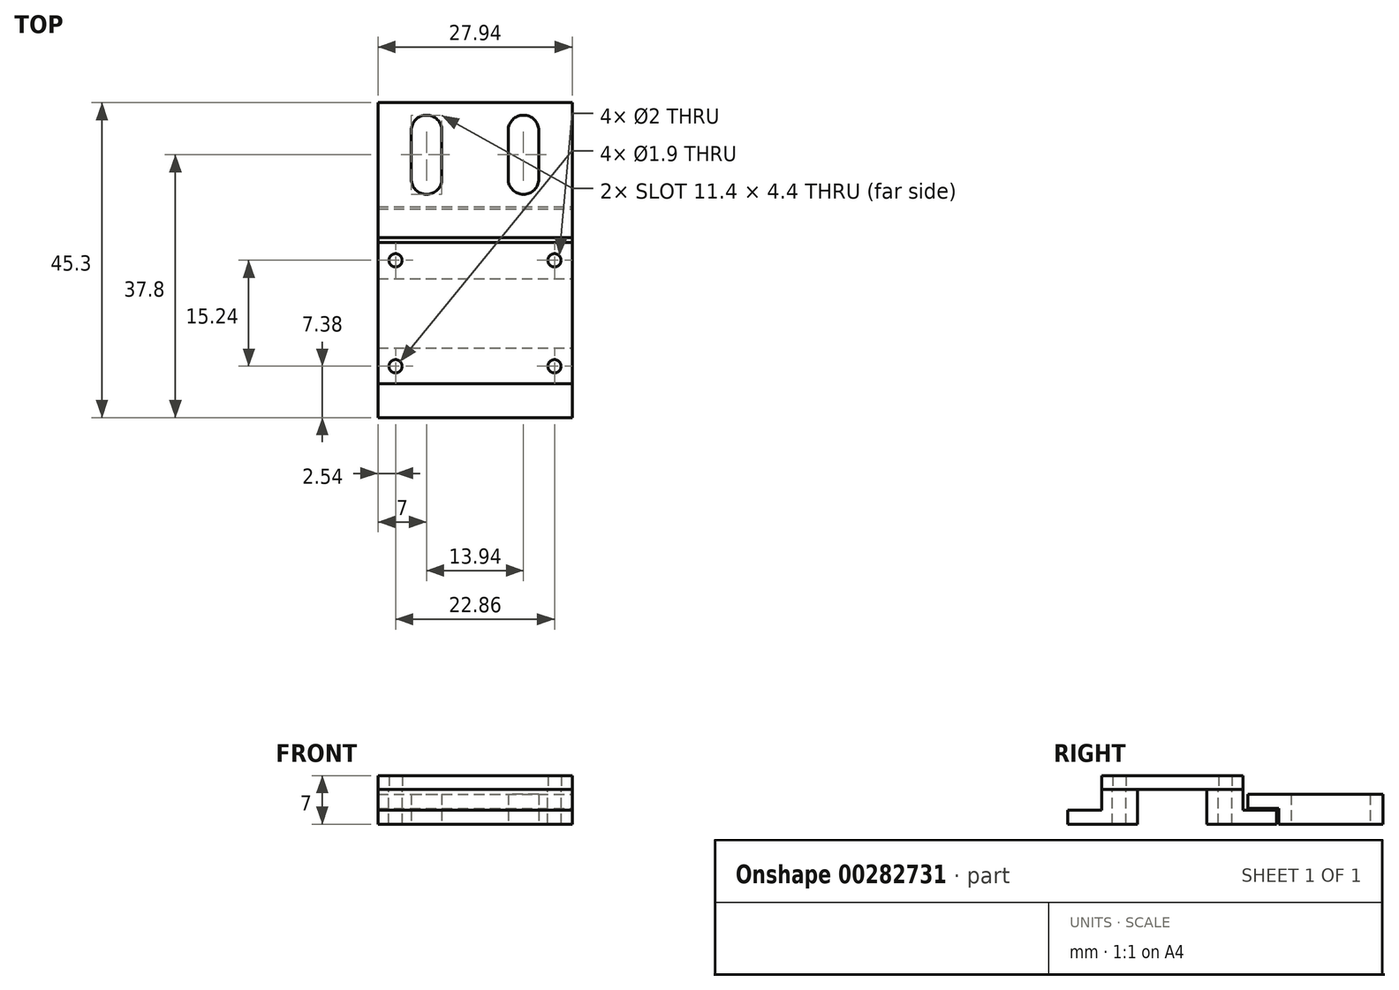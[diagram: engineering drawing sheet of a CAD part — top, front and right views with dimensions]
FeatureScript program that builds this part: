
annotation { "Feature Type Name" : "Feature", "Feature Type Description" : "" }
export const myFeature = defineFeature(function(context is Context, id is Id, definition is map)
    precondition{}
    {
        {
            var Q0;
            Q0=qCreatedBy(makeId("Top.planeOp"),FACE);
            var sketch = newSketch(context, id + "F0", { "sketchPlane" : qUnion([Q0])});
            skLineSegment(sketch, "E0.bottom", {"start": v(13.97, -10.16) * mm, "end": v(-13.97, -10.16) * mm});
            skLineSegment(sketch, "E0.top", {"start": v(13.97, 10.16) * mm, "end": v(-13.97, 10.16) * mm});
            skLineSegment(sketch, "E0.left", {"start": v(13.97, -10.16) * mm, "end": v(13.97, 10.16) * mm});
            skLineSegment(sketch, "E0.right", {"start": v(-13.97, -10.16) * mm, "end": v(-13.97, 10.16) * mm});
            skPoint(sketch, "E0.middle", {"position": v(0, 0) * mm});
            skLineSegment(sketch, "E1.bottom", {"start": v(11.43, -7.62) * mm, "end": v(-11.43, -7.62) * mm, "construction": true});
            skLineSegment(sketch, "E1.top", {"start": v(11.43, 7.62) * mm, "end": v(-11.43, 7.62) * mm, "construction": true});
            skLineSegment(sketch, "E1.left", {"start": v(11.43, -7.62) * mm, "end": v(11.43, 7.62) * mm, "construction": true});
            skLineSegment(sketch, "E1.right", {"start": v(-11.43, -7.62) * mm, "end": v(-11.43, 7.62) * mm, "construction": true});
            skCircle(sketch, "E2", {"center": v(-11.43, 7.62) * mm, "radius": 0.95 * mm});
            skCircle(sketch, "E3", {"center": v(-11.43, -7.62) * mm, "radius": 0.95 * mm});
            skCircle(sketch, "E4", {"center": v(11.43, 7.62) * mm, "radius": 0.95 * mm});
            skCircle(sketch, "E5", {"center": v(11.43, -7.62) * mm, "radius": 0.95 * mm});
            skSolve(sketch);
        }
        {
            var Q0;
            Q0 = qSketchRegion(id + "F0", true);
            extrude(context, id + "F1", {"entities" : qUnion([Q0]), "depth" : 2 * mm});
        }
        {
            var Q0;
            Q0=makeQuery(id+"F0.imprint","IMPRINT",FACE,{"disambiguationData":[TD([[makeQuery(id+"F0.imprint","IMPRINT",EDGE,{"derivedFrom":sQuery(id+"F0.wireOp",EDGE,"E0.bottom")}),-1.0]])]});
            var sketch = newSketch(context, id + "F2", { "sketchPlane" : qUnion([Q0])});
            skLineSegment(sketch, "E6.top", {"start": v(-13.97, -10.16) * mm, "end": v(13.97, -10.16) * mm});
            skLineSegment(sketch, "E6.left", {"start": v(-13.97, -5) * mm, "end": v(-13.97, -10.16) * mm});
            skLineSegment(sketch, "E6.right", {"start": v(13.97, -5) * mm, "end": v(13.97, -10.16) * mm});
            skLineSegment(sketch, "E7", {"start": v(-13.97, -5) * mm, "end": v(13.97, -5) * mm});
            skLineSegment(sketch, "E8.MirrorCS", {"start": v(-13.97, 10.16) * mm, "end": v(13.97, 10.16) * mm});
            skLineSegment(sketch, "E9.MirrorCS", {"start": v(-13.97, 5) * mm, "end": v(-13.97, 10.16) * mm});
            skLineSegment(sketch, "E10.MirrorCS", {"start": v(-13.97, 5) * mm, "end": v(13.97, 5) * mm});
            skLineSegment(sketch, "E11.MirrorCS", {"start": v(13.97, 5) * mm, "end": v(13.97, 10.16) * mm});
            skSolve(sketch);
        }
        {
            var Q0;
            Q0 = qSketchRegion(id + "F2", true);
            extrude(context, id + "F3", {"entities" : qUnion([Q0]), "oppositeDirection" : true, "depth" : 3 * mm});
        }
        {
            var Q0;
            Q0=makeQuery(id+"F3.opExtrude","CAP_FACE",FACE,{"disambiguationData":[OSD([sQuery(id+"F2.wireOp",EDGE,"E6.top"),sQuery(id+"F2.wireOp",EDGE,"E6.left"),sQuery(id+"F2.wireOp",EDGE,"E6.right"),sQuery(id+"F2.wireOp",EDGE,"E7")])],"isStart":false});
            var sketch = newSketch(context, id + "F4", { "sketchPlane" : qUnion([Q0])});
            skLineSegment(sketch, "E12.bottom", {"start": v(-13.97, 5) * mm, "end": v(13.97, 5) * mm});
            skLineSegment(sketch, "E12.top", {"start": v(-13.97, 15) * mm, "end": v(13.97, 15) * mm});
            skLineSegment(sketch, "E12.left", {"start": v(-13.97, 5) * mm, "end": v(-13.97, 15) * mm});
            skLineSegment(sketch, "E12.right", {"start": v(13.97, 5) * mm, "end": v(13.97, 15) * mm});
            skSolve(sketch);
        }
        {
            var Q0;
            Q0 = qSketchRegion(id + "F4", true);
            extrude(context, id + "F5", {"entities" : qUnion([Q0]), "operationType" : NewBodyOperationType.ADD, "depth" : 2 * mm});
        }
        {
            var Q0;
            Q0=makeQuery(id+"F3.opExtrude","CAP_FACE",FACE,{"disambiguationData":[OSD([sQuery(id+"F2.wireOp",EDGE,"E8.MirrorCS"),sQuery(id+"F2.wireOp",EDGE,"E9.MirrorCS"),sQuery(id+"F2.wireOp",EDGE,"E10.MirrorCS"),sQuery(id+"F2.wireOp",EDGE,"E11.MirrorCS")])],"isStart":false});
            var sketch = newSketch(context, id + "F6", { "sketchPlane" : qUnion([Q0])});
            skLineSegment(sketch, "E13.bottom", {"start": v(-13.97, -5) * mm, "end": v(13.97, -5) * mm});
            skLineSegment(sketch, "E13.top", {"start": v(-13.97, -15) * mm, "end": v(13.97, -15) * mm});
            skLineSegment(sketch, "E13.left", {"start": v(-13.97, -5) * mm, "end": v(-13.97, -15) * mm});
            skLineSegment(sketch, "E13.right", {"start": v(13.97, -5) * mm, "end": v(13.97, -15) * mm});
            skSolve(sketch);
        }
        {
            var Q0;
            Q0 = qSketchRegion(id + "F6", true);
            extrude(context, id + "F7", {"entities" : qUnion([Q0]), "operationType" : NewBodyOperationType.ADD, "depth" : 2 * mm});
        }
        {
            var Q0;
            Q0=makeQuery(id+"F7.opExtrude","CAP_FACE",FACE,{"disambiguationData":[OSD([sQuery(id+"F6.wireOp",EDGE,"E13.bottom"),sQuery(id+"F6.wireOp",EDGE,"E13.top"),sQuery(id+"F6.wireOp",EDGE,"E13.left"),sQuery(id+"F6.wireOp",EDGE,"E13.right")])],"isStart":false});
            var sketch = newSketch(context, id + "F8", { "sketchPlane" : qUnion([Q0])});
            skLineSegment(sketch, "E14.bottom", {"start": v(-13.97, -15.3) * mm, "end": v(13.97, -15.3) * mm});
            skLineSegment(sketch, "E14.top", {"start": v(-13.97, -30.3) * mm, "end": v(13.97, -30.3) * mm});
            skLineSegment(sketch, "E14.left", {"start": v(-13.97, -15.3) * mm, "end": v(-13.97, -30.3) * mm});
            skLineSegment(sketch, "E14.right", {"start": v(13.97, -15.3) * mm, "end": v(13.97, -30.3) * mm});
            skLineSegment(sketch, "E15", {"start": v(-13.97, -22.8) * mm, "end": v(13.97, -22.8) * mm, "construction": true});
            skLineSegment(sketch, "E16", {"start": v(-6.97, -15.3) * mm, "end": v(-6.97, -30.3) * mm, "construction": true});
            skLineSegment(sketch, "E17", {"start": v(6.97, -15.3) * mm, "end": v(6.97, -30.3) * mm, "construction": true});
            skPoint(sketch, "E18", {"position": v(-6.97, -22.8) * mm});
            skPoint(sketch, "E19", {"position": v(6.97, -22.8) * mm});
            skPoint(sketch, "E20", {"position": v(-6.97, -19.3) * mm});
            skPoint(sketch, "E21", {"position": v(-6.97, -26.3) * mm});
            skArc(sketch, "E22", {"start": v(-4.77, -19.3) * mm, "mid": v(-6.97, -17.1) * mm, "end": v(-9.17, -19.3) * mm});
            skArc(sketch, "E23", {"start": v(-9.17, -26.3) * mm, "mid": v(-6.97, -28.5) * mm, "end": v(-4.77, -26.3) * mm});
            skLineSegment(sketch, "E24", {"start": v(-9.17, -19.3) * mm, "end": v(-9.17, -26.3) * mm});
            skLineSegment(sketch, "E25", {"start": v(-4.77, -19.3) * mm, "end": v(-4.77, -26.3) * mm});
            skLineSegment(sketch, "E26.MirrorCS", {"start": v(9.17, -19.3) * mm, "end": v(9.17, -26.3) * mm});
            skLineSegment(sketch, "E27.MirrorCS", {"start": v(4.77, -19.3) * mm, "end": v(4.77, -26.3) * mm});
            skArc(sketch, "E28.MirrorCS", {"start": v(4.77, -19.3) * mm, "mid": v(6.97, -17.1) * mm, "end": v(9.17, -19.3) * mm});
            skArc(sketch, "E29.MirrorCS", {"start": v(9.17, -26.3) * mm, "mid": v(6.97, -28.5) * mm, "end": v(4.77, -26.3) * mm});
            skSolve(sketch);
        }
        {
            var Q0;
            Q0 = qSketchRegion(id + "F8", true);
            extrude(context, id + "F9", {"entities" : qUnion([Q0]), "oppositeDirection" : true, "depth" : 2.3 * mm});
        }
        {
            var Q0;
            Q0=makeQuery(id+"F9.opExtrude","CAP_FACE",FACE,{"disambiguationData":[OSD([sQuery(id+"F8.wireOp",EDGE,"E14.bottom"),sQuery(id+"F8.wireOp",EDGE,"E14.top"),sQuery(id+"F8.wireOp",EDGE,"E14.left"),sQuery(id+"F8.wireOp",EDGE,"E14.right")])],"isStart":false});
            var sketch = newSketch(context, id + "F10", { "sketchPlane" : qUnion([Q0])});
            skLineSegment(sketch, "E30.bottom", {"start": v(13.97, 30.3) * mm, "end": v(-13.97, 30.3) * mm});
            skLineSegment(sketch, "E30.top", {"start": v(13.97, 10.9) * mm, "end": v(-13.97, 10.9) * mm});
            skLineSegment(sketch, "E30.left", {"start": v(13.97, 30.3) * mm, "end": v(13.97, 10.9) * mm});
            skLineSegment(sketch, "E30.right", {"start": v(-13.97, 30.3) * mm, "end": v(-13.97, 10.9) * mm});
            skSolve(sketch);
        }
        {
            var Q0;
            Q0 = qSketchRegion(id + "F10", true);
            extrude(context, id + "F11", {"entities" : qUnion([Q0]), "operationType" : NewBodyOperationType.ADD, "depth" : 2 * mm});
        }
        {
            var Q0;
            Q0=sQuery(id+"F0.wireOp",VERTEX,"E2.center");
            var Q1;
            Q1=sQuery(id+"F0.wireOp",VERTEX,"E1.top.start");
            var Q2;
            Q2=sQuery(id+"F0.wireOp",VERTEX,"E5.center");
            var Q3;
            Q3=sQuery(id+"F0.wireOp",VERTEX,"E1.bottom.end");
            var Q4;
            Q4=makeQuery(id+"F3.opExtrude","SWEPT_BODY",BODY,{"disambiguationData":[OSD([sQuery(id+"F2.wireOp",EDGE,"E6.top"),sQuery(id+"F2.wireOp",EDGE,"E6.left"),sQuery(id+"F2.wireOp",EDGE,"E6.right"),sQuery(id+"F2.wireOp",EDGE,"E7")])]});
            var Q5;
            Q5=makeQuery(id+"F3.opExtrude","SWEPT_BODY",BODY,{"disambiguationData":[OSD([sQuery(id+"F2.wireOp",EDGE,"E8.MirrorCS"),sQuery(id+"F2.wireOp",EDGE,"E9.MirrorCS"),sQuery(id+"F2.wireOp",EDGE,"E10.MirrorCS"),sQuery(id+"F2.wireOp",EDGE,"E11.MirrorCS")])]});
            hole(context, id + "F12", {"style" : HoleStyle.SIMPLE, "endStyle" : HoleEndStyle.BLIND, "holeDiameter" : 2 * mm, "holeDepth" : 20 * mm, "tappedDepth" : 12 * mm, "tapClearance" : 3, "startFromSketch" : true, "locations" : qUnion([Q0, Q1, Q2, Q3]), "scope" : qUnion([Q4, Q5])});
        }
        {
            var Q0;
            Q0=sQuery(id+"F8.wireOp",VERTEX,"E18");
            var Q1;
            Q1=sQuery(id+"F8.wireOp",VERTEX,"E19");
            var Q2;
            Q2=makeQuery(id+"F9.opExtrude","SWEPT_BODY",BODY,{"disambiguationData":[OSD([sQuery(id+"F8.wireOp",EDGE,"E14.bottom"),sQuery(id+"F8.wireOp",EDGE,"E14.top"),sQuery(id+"F8.wireOp",EDGE,"E14.left"),sQuery(id+"F8.wireOp",EDGE,"E14.right")])]});
            hole(context, id + "F13", {"style" : HoleStyle.SIMPLE, "endStyle" : HoleEndStyle.BLIND, "standardTappedOrClearance" : lookupTablePath({ "standard" : "ISO", "fit" : "Normal", "size" : "M4", "type" : "Clearance" }), "standardBlindInLast" : lookupTablePath({ "fit" : "Standard", "standard" : "ISO", "size" : "M4", "type" : "Clearance" }), "holeDiameter" : 4.4 * mm, "holeDepth" : 20 * mm, "tappedDepth" : 12 * mm, "tapClearance" : 3, "locations" : qUnion([Q0, Q1]), "scope" : qUnion([Q2])});
        }
        {
            var Q0;
            Q0=makeQuery(id+"F8.imprint","IMPRINT",FACE,{"disambiguationData":[TD([[makeQuery(id+"F8.imprint","IMPRINT",EDGE,{"derivedFrom":sQuery(id+"F8.wireOp",EDGE,"E26.MirrorCS")}),-1.0]])]});
            var Q1;
            Q1=makeQuery(id+"F8.imprint","IMPRINT",FACE,{"disambiguationData":[TD([[makeQuery(id+"F8.imprint","IMPRINT",EDGE,{"derivedFrom":sQuery(id+"F8.wireOp",EDGE,"E22")}),1.0]])]});
            extrude(context, id + "F14", {"entities" : qUnion([Q0, Q1]), "operationType" : NewBodyOperationType.REMOVE, "oppositeDirection" : true, "depth" : 25 * mm});
        }
    });
